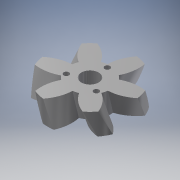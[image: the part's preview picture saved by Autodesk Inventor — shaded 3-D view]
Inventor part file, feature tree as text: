
AUTODESK INVENTOR PART (.ipt)
format: ipt  version: 2017 SP1 (Build 210196100, 196)  size: 582,144 bytes
history: native  units: mm (DEFAULTED — no unit token found)
features: sketch x4, plane x3, other x3, extrude x2, hole x1
ambient origin geometry x8: Origin, YZ Plane, XZ Plane, XY Plane, X Axis, Y Axis, Z Axis, Center Point
bodies: Solid1 (feature_tree)
feature tree (13):
  extrude  "Extrusion1"  Depth=10.0mm TaperAngle=0.0deg
  plane  "Work Plane2"
  plane  "Work Plane8"
  plane  "Work Plane9"
  other  "Engrenage cylindrique"
  extrude  "Extrusion2"  Depth=10.0mm TaperAngle=0.0deg
  hole  "Perçage1"  [1 undecoded]
  sketch  "Sketch1"  dims[d0=38.885336mm d1=10.0mm d2=0.0mm]
  sketch  "Sketch2"  dims[d3=30.066593mm d4=10.0mm d5=0.0mm d16=30.066593mm d17=0.0mm d34=30.0deg d39=0.0mm d41=0.0mm d43=30.066593mm d46=30.066593mm d47=0.0mm d48=0.0mm d49=8.0mm d50=10.0mm d51=0.0mm d52=8.0mm d53=30.0mm d55=360.0deg d57=2.5mm d58=6.0mm d59=4.0mm d60=2.0mm d61=90.0deg d62=8.0mm d63=20.594885mm]
  other  "Srf1"
  sketch  "Esquisse3"
  sketch  "Esquisse4"
  other  "Diamètre primitif"
note: 1 required parameter value undecoded (feature->parameter linkage not recoverable at this tier; creation-order binding heuristic only, values carry confidence <= 0.55)
